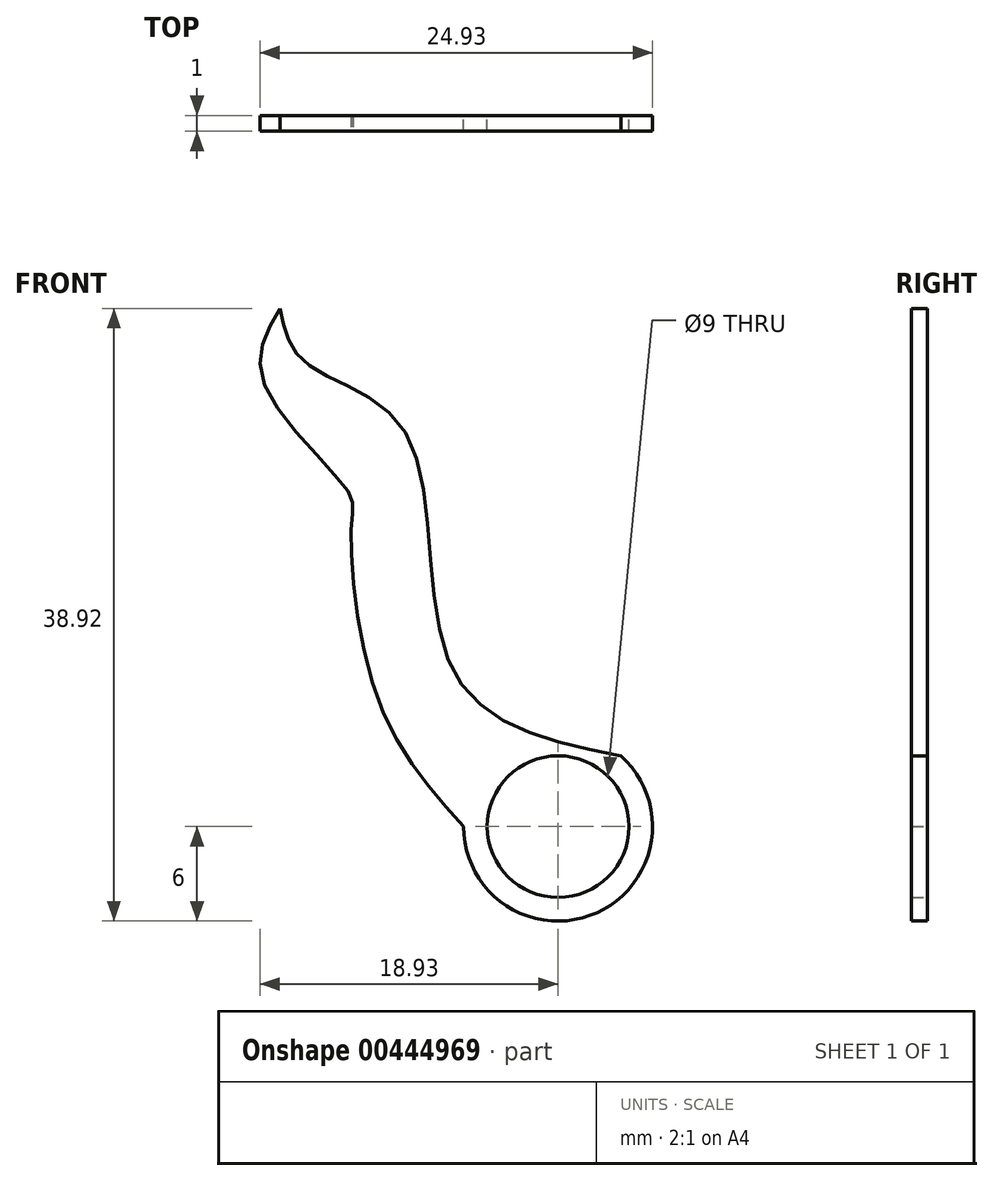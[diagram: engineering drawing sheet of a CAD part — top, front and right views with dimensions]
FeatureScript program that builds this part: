
annotation { "Feature Type Name" : "Feature", "Feature Type Description" : "" }
export const myFeature = defineFeature(function(context is Context, id is Id, definition is map)
    precondition{}
    {
        {
            var Q0;
            Q0=qCreatedBy(makeId("Front.planeOp"),FACE);
            var sketch = newSketch(context, id + "F0", { "sketchPlane" : qUnion([Q0])});
            skCircle(sketch, "E0", {"center": v(0, 0) * mm, "radius": 4.5 * mm});
            skArc(sketch, "E1", {"start": v(-6, 0) * mm, "mid": v(2.46, -5.47) * mm, "end": v(3.98, 4.49) * mm});
            skFitSpline(sketch, "E2", {"points": [v(-6, 0) * mm, v(-11.5, 8.26) * mm, v(-13.12, 19.41) * mm, v(-13.28, 21.2) * mm, v(-18.7, 28.23) * mm, v(-17.65, 32.92) * mm], "startDerivative": vector(-26.17, 28.9) * mm, "endDerivative": vector(15.15, 25.67) * mm});
            skFitSpline(sketch, "E3", {"points": [v(3.98, 4.49) * mm, v(-6.65, 9.87) * mm, v(-9.72, 25.07) * mm, v(-16.11, 29.52) * mm, v(-17.65, 32.92) * mm], "startDerivative": vector(-46.28, 9.57) * mm, "endDerivative": vector(-4.4, 23.46) * mm});
            skSolve(sketch);
        }
        {
            var Q0;
            Q0 = qSketchRegion(id + "F0", true);
            extrude(context, id + "F1", {"entities" : qUnion([Q0]), "depth" : 1 * mm});
        }
    });
